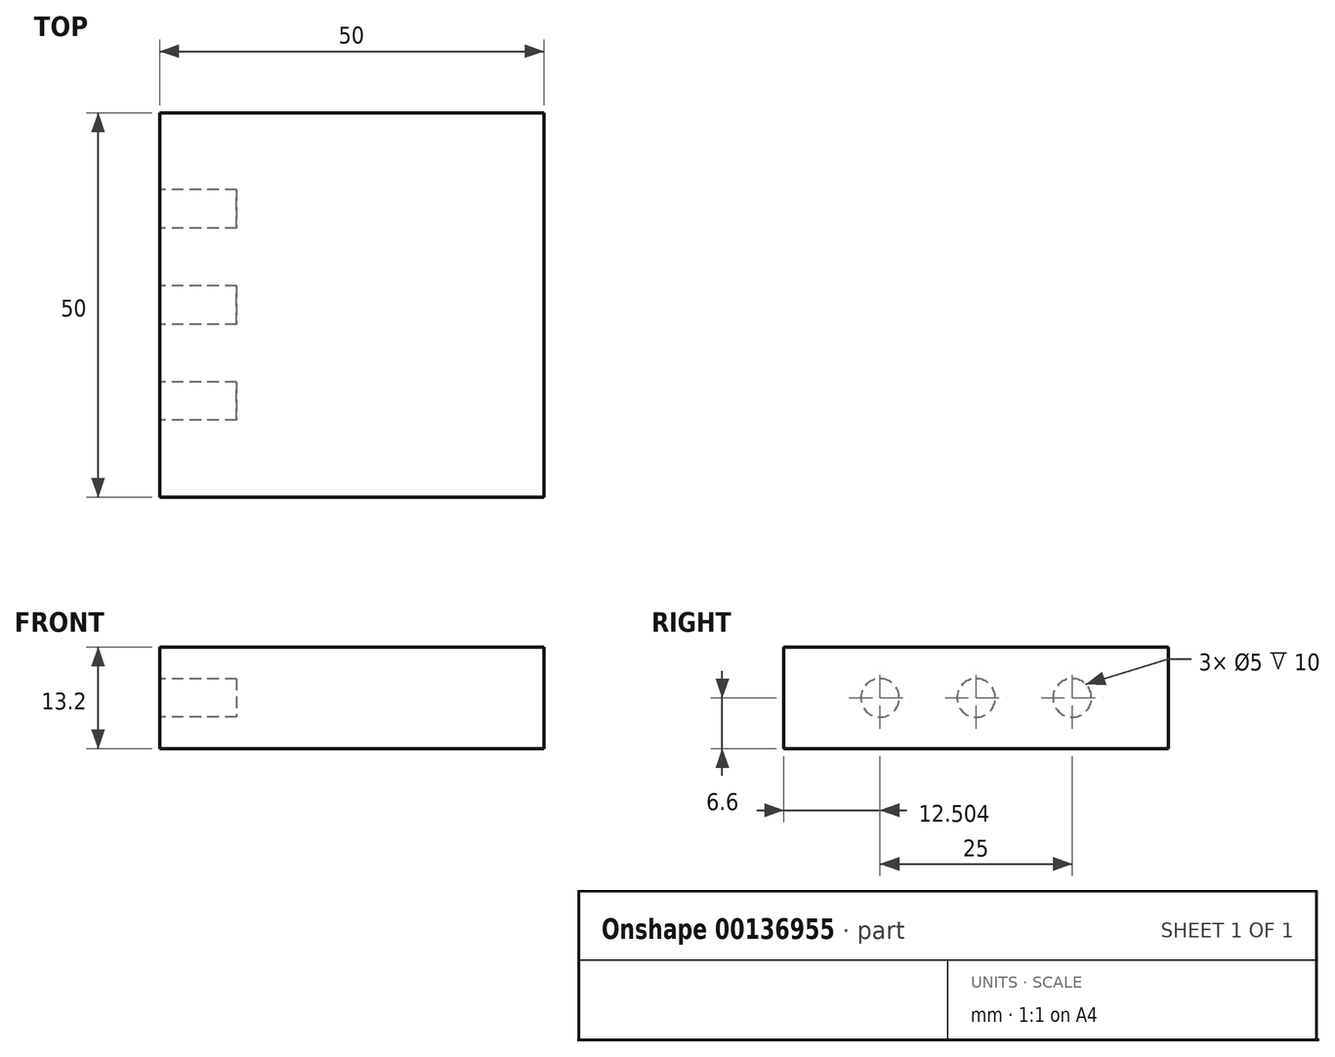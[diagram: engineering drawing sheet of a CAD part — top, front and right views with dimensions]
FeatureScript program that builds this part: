
annotation { "Feature Type Name" : "Feature", "Feature Type Description" : "" }
export const myFeature = defineFeature(function(context is Context, id is Id, definition is map)
    precondition{}
    {
        {
            var Q0;
            Q0=qCreatedBy(makeId("Top.planeOp"),FACE);
            var sketch = newSketch(context, id + "F0", { "sketchPlane" : qUnion([Q0])});
            skLineSegment(sketch, "E0.bottom", {"start": v(-22.1, 10.26) * mm, "end": v(27.9, 10.26) * mm});
            skLineSegment(sketch, "E0.top", {"start": v(-22.1, -39.74) * mm, "end": v(27.9, -39.74) * mm});
            skLineSegment(sketch, "E0.left", {"start": v(-22.1, 10.26) * mm, "end": v(-22.1, -39.74) * mm});
            skLineSegment(sketch, "E0.right", {"start": v(27.9, 10.26) * mm, "end": v(27.9, -39.74) * mm});
            skLineSegment(sketch, "E1.filletArc", {"start": v(-22.1, 10.26) * mm, "end": v(-22.1, 10.26) * mm});
            skPoint(sketch, "E2.visualSharp", {"position": v(27.9, 10.26) * mm});
            skLineSegment(sketch, "E2.filletArc", {"start": v(27.9, 10.26) * mm, "end": v(27.9, 10.26) * mm});
            skPoint(sketch, "E3.visualSharp", {"position": v(27.9, -39.74) * mm});
            skLineSegment(sketch, "E3.filletArc", {"start": v(27.9, -39.74) * mm, "end": v(27.9, -39.74) * mm});
            skPoint(sketch, "E4.visualSharp", {"position": v(-22.1, -39.74) * mm});
            skLineSegment(sketch, "E4.filletArc", {"start": v(-22.1, -39.74) * mm, "end": v(-22.1, -39.74) * mm});
            skSolve(sketch);
        }
        {
            var Q0;
            Q0=makeQuery(id+"F0.imprint","IMPRINT",FACE,{"disambiguationData":[TD([[makeQuery(id+"F0.imprint","IMPRINT",EDGE,{"derivedFrom":sQuery(id+"F0.wireOp",EDGE,"E0.bottom")}),-1.0]])]});
            extrude(context, id + "F1", {"entities" : qUnion([Q0]), "depth" : 13.2 * mm, "offsetDistance" : 25 * mm});
        }
        {
            var Q0;
            Q0=makeQuery(id+"F1.opExtrude","SWEPT_FACE",FACE,{"disambiguationData":[OSD([sQuery(id+"F0.wireOp",EDGE,"E0.left")])]});
            var sketch = newSketch(context, id + "F2", { "sketchPlane" : qUnion([Q0])});
            skCircle(sketch, "E5", {"center": v(14.74, 6.6) * mm, "radius": 2.5 * mm});
            skPoint(sketch, "E6.startSnap0", {"position": v(2.24, 6.6) * mm});
            skPoint(sketch, "E7.startSnap0", {"position": v(27.24, 6.6) * mm});
            skCircle(sketch, "E8", {"center": v(2.24, 6.6) * mm, "radius": 2.5 * mm});
            skCircle(sketch, "E9", {"center": v(27.24, 6.6) * mm, "radius": 2.5 * mm});
            skSolve(sketch);
        }
        {
            var Q0;
            Q0=makeQuery(id+"F2.imprint","IMPRINT",FACE,{"disambiguationData":[TD([[makeQuery(id+"F2.imprint","IMPRINT",EDGE,{"derivedFrom":sQuery(id+"F2.wireOp",EDGE,"E8")}),1.0]])]});
            var Q1;
            Q1=makeQuery(id+"F2.imprint","IMPRINT",FACE,{"disambiguationData":[TD([[makeQuery(id+"F2.imprint","IMPRINT",EDGE,{"derivedFrom":sQuery(id+"F2.wireOp",EDGE,"E5")}),1.0]])]});
            var Q2;
            Q2=makeQuery(id+"F2.imprint","IMPRINT",FACE,{"disambiguationData":[TD([[makeQuery(id+"F2.imprint","IMPRINT",EDGE,{"derivedFrom":sQuery(id+"F2.wireOp",EDGE,"E9")}),1.0]])]});
            extrude(context, id + "F3", {"entities" : qUnion([Q0, Q1, Q2]), "operationType" : NewBodyOperationType.REMOVE, "oppositeDirection" : true, "depth" : 10 * mm, "offsetDistance" : 25 * mm});
        }
    });
